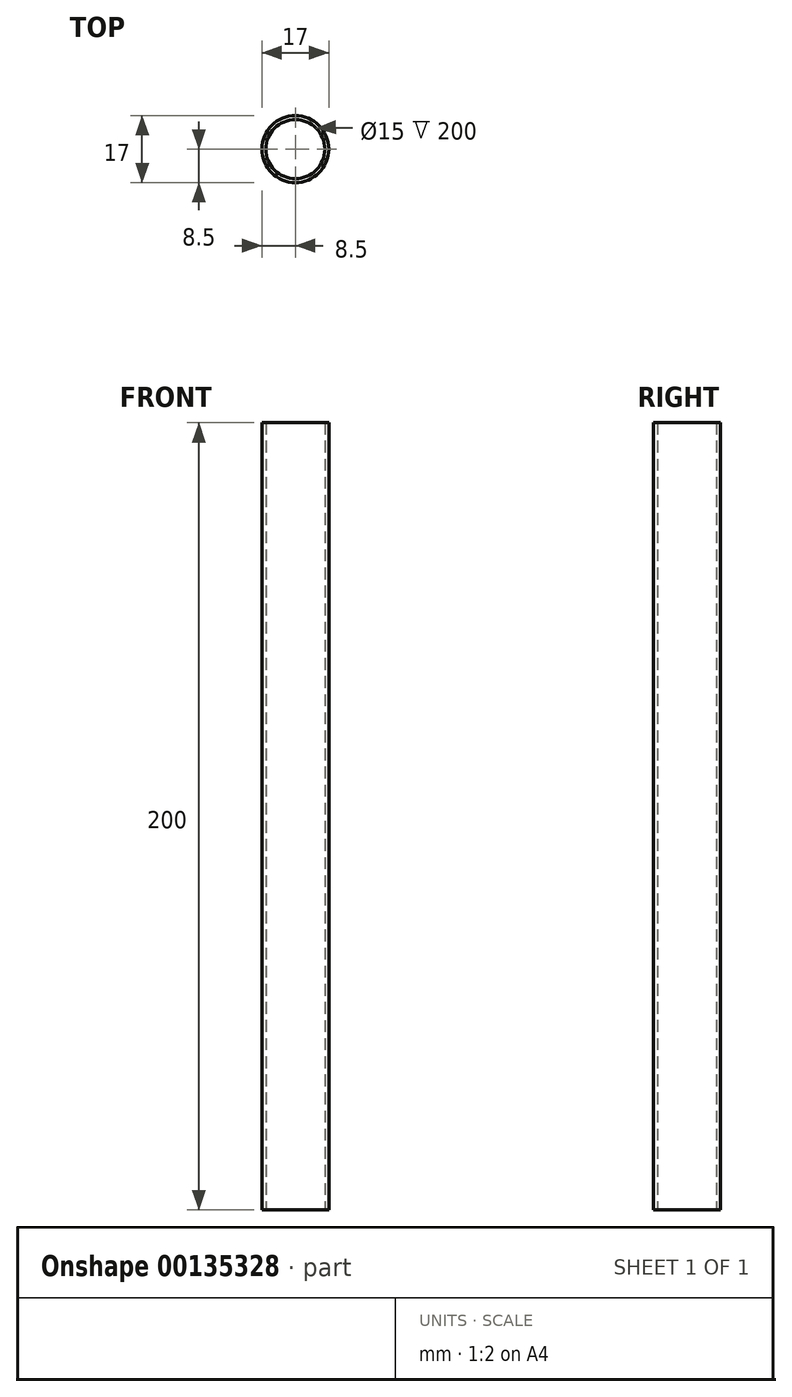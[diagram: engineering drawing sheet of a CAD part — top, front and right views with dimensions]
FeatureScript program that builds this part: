
annotation { "Feature Type Name" : "Feature", "Feature Type Description" : "" }
export const myFeature = defineFeature(function(context is Context, id is Id, definition is map)
    precondition{}
    {
        {
            var Q0;
            Q0=qCreatedBy(makeId("Top.planeOp"),FACE);
            var sketch = newSketch(context, id + "F0", { "sketchPlane" : qUnion([Q0])});
            skCircle(sketch, "E0", {"center": v(0, 0) * mm, "radius": 7.5 * mm});
            skCircle(sketch, "E1.0", {"center": v(0, 0) * mm, "radius": 8.5 * mm});
            skSolve(sketch);
        }
        {
            var Q0;
            Q0=makeQuery(id+"F0.imprint","IMPRINT",FACE,{"disambiguationData":[TD([[makeQuery(id+"F0.imprint","IMPRINT",EDGE,{"derivedFrom":sQuery(id+"F0.wireOp",EDGE,"E0")}),-1.0]])]});
            extrude(context, id + "F1", {"entities" : qUnion([Q0]), "depth" : 200 * mm});
        }
    });
